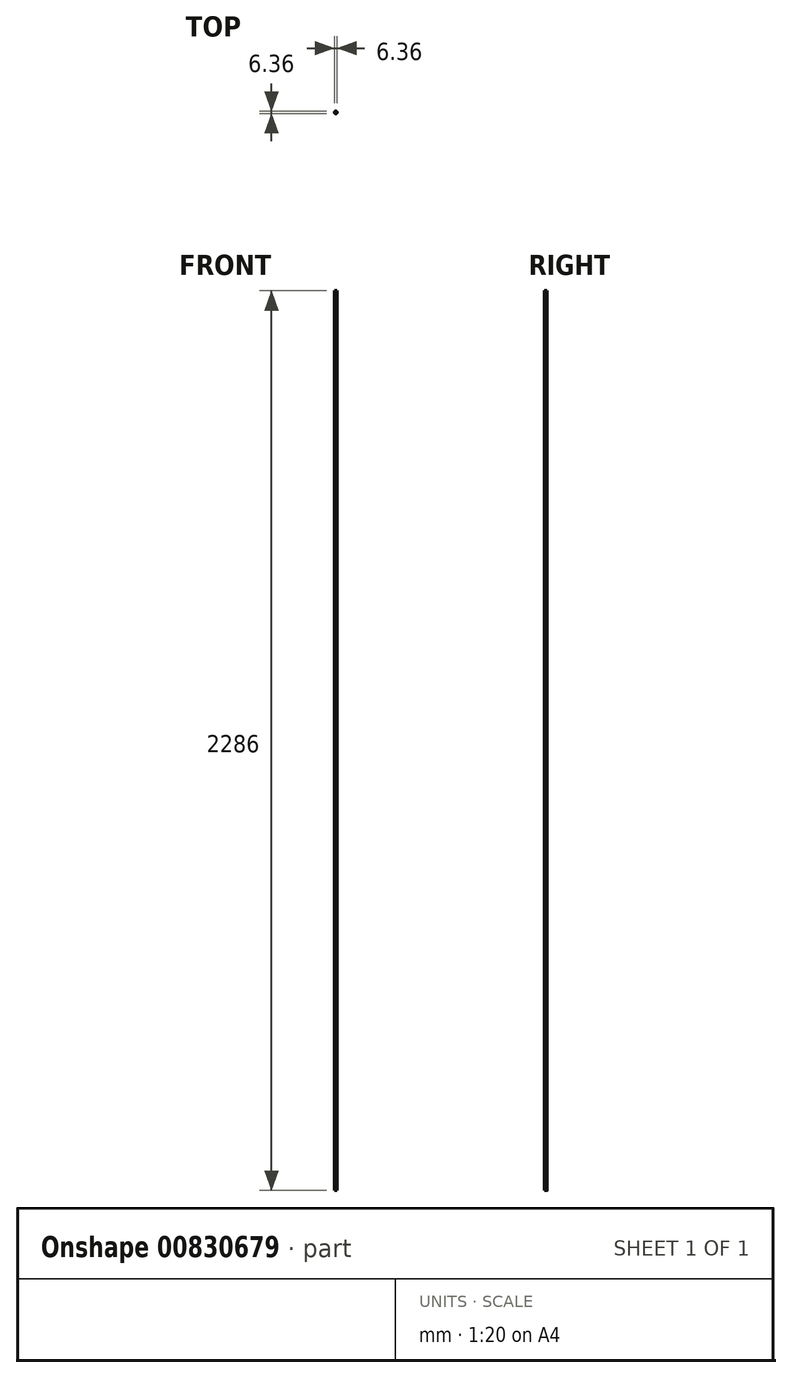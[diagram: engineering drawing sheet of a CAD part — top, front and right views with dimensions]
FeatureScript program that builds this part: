
annotation { "Feature Type Name" : "Feature", "Feature Type Description" : "" }
export const myFeature = defineFeature(function(context is Context, id is Id, definition is map)
    precondition{}
    {
        {
            var Q0;
            Q0=qCreatedBy(makeId("Top.planeOp"),FACE);
            var sketch = newSketch(context, id + "F0", { "sketchPlane" : qUnion([Q0])});
            skCircle(sketch, "E0", {"center": v(0, 0) * mm, "radius": 3.18 * mm});
            skSolve(sketch);
        }
        {
            var Q0;
            Q0 = qSketchRegion(id + "F0", true);
            extrude(context, id + "F1", {"entities" : qUnion([Q0]), "depth" : 2286 * mm, "offsetDistance" : 25.4 * mm});
        }
    });
